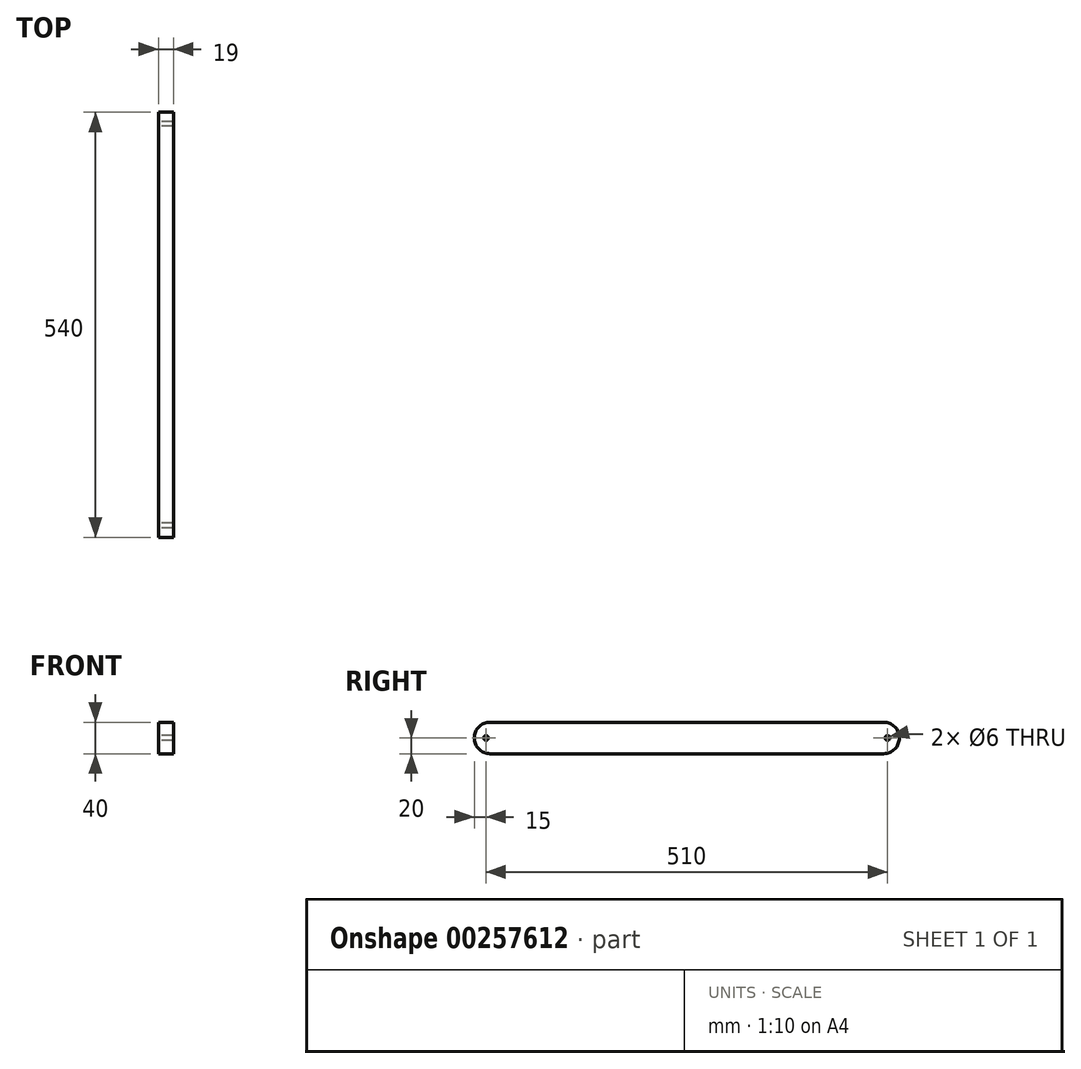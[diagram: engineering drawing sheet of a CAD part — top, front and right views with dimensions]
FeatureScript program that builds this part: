
annotation { "Feature Type Name" : "Feature", "Feature Type Description" : "" }
export const myFeature = defineFeature(function(context is Context, id is Id, definition is map)
    precondition{}
    {
        {
            var Q0;
            Q0=qCreatedBy(makeId("Right.planeOp"),FACE);
            var sketch = newSketch(context, id + "F0", { "sketchPlane" : qUnion([Q0])});
            skCircle(sketch, "E0", {"center": v(0, 0) * mm, "radius": 3 * mm});
            skCircle(sketch, "E1", {"center": v(-510, 0) * mm, "radius": 3 * mm});
            skLineSegment(sketch, "E2.bottom", {"start": v(-525, 20) * mm, "end": v(15, 20) * mm});
            skLineSegment(sketch, "E2.top", {"start": v(-525, -20) * mm, "end": v(15, -20) * mm});
            skLineSegment(sketch, "E2.left", {"start": v(-525, 20) * mm, "end": v(-525, -20) * mm});
            skLineSegment(sketch, "E2.right", {"start": v(15, 20) * mm, "end": v(15, -20) * mm});
            skSolve(sketch);
        }
        {
            var Q0;
            Q0=qSketchRegion(id+"F0",true);
            extrude(context, id + "F1", {"entities" : qUnion([Q0]), "depth" : 19 * mm});
        }
        {
            var Q0;
            Q0=makeQuery(id+"F1.opExtrude","SWEPT_EDGE",EDGE,{"disambiguationData":[OSD([sQuery(id+"F0.wireOp",EDGE,"E2.bottom"),sQuery(id+"F0.wireOp",EDGE,"E2.right")])]});
            var Q1;
            Q1=makeQuery(id+"F1.opExtrude","SWEPT_EDGE",EDGE,{"disambiguationData":[OSD([sQuery(id+"F0.wireOp",EDGE,"E2.top"),sQuery(id+"F0.wireOp",EDGE,"E2.right")])]});
            var Q2;
            Q2=makeQuery(id+"F1.opExtrude","SWEPT_EDGE",EDGE,{"disambiguationData":[OSD([sQuery(id+"F0.wireOp",EDGE,"E2.bottom"),sQuery(id+"F0.wireOp",EDGE,"E2.left")])]});
            var Q3;
            Q3=makeQuery(id+"F1.opExtrude","SWEPT_EDGE",EDGE,{"disambiguationData":[OSD([sQuery(id+"F0.wireOp",EDGE,"E2.top"),sQuery(id+"F0.wireOp",EDGE,"E2.left")])]});
            fillet(context, id + "F2", {"entities" : qUnion([Q0, Q1, Q2, Q3]), "radius" : 20 * mm, "tangentPropagation" : true, "allowEdgeOverflow" : false});
        }
    });
